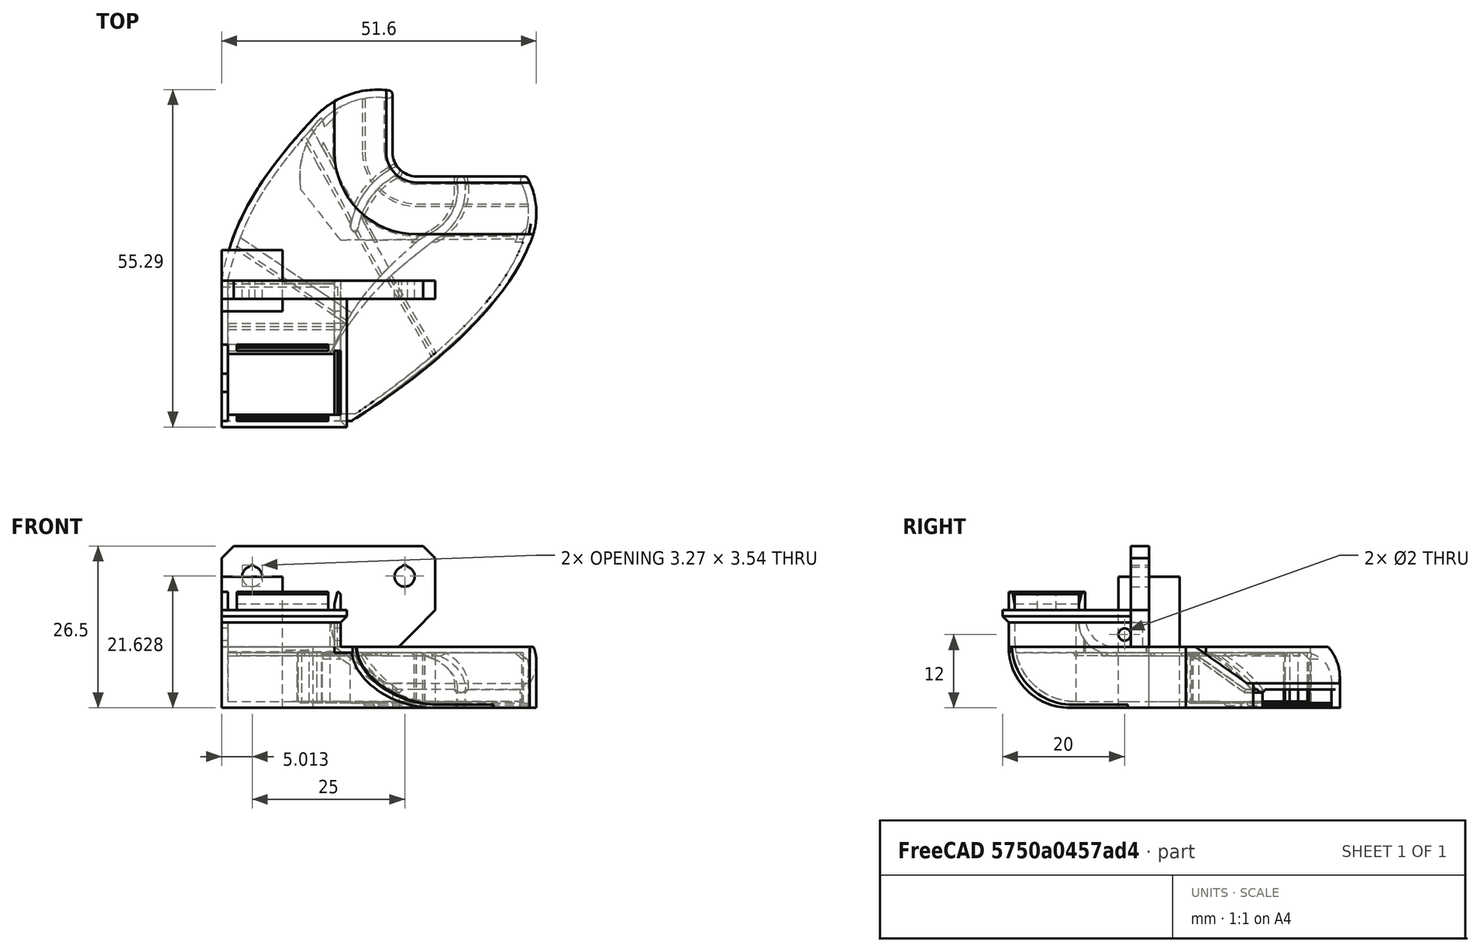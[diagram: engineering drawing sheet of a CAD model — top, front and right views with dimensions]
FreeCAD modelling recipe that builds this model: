
FCSTD DOCUMENT  (FreeCAD 0.18R16146 (Git))
Label: tidan-duct
License: All rights reserved
LicenseURL: http://en.wikipedia.org/wiki/All_rights_reserved
objects: Part::Box×37, Part::Cut×24, Part::Chamfer×18, Part::Feature×14, Part::MultiFuse×11, Part::Cylinder×6, Part::Fillet×6
note: 116 computed .brp shape members not serialized (recipe doc carries the construction recipe); baked Part::Feature solids carry a one-line shape summary decoded from their .brp

FEATURE [Part::Feature] Part__Feature034001  label="duct001"
  Placement = pos=(4.485,21.775,-6.0908e-11) rot=(0,0,-1;0.785398rad)
  shape: bbox 54.56 x 52.76 x 17.07 mm, 140 faces (baked)
FEATURE [Part::Box] Box  label="Cube"
  AttacherType = Attacher::AttachEngine3D
  Height = 10
  Length = 42
  Placement = pos=(-35,-33,10) rot=(0,0,1;0rad)
  Width = 47
FEATURE [Part::Cut] Cut
  Base = -> Part__Feature034001
  Tool = -> Box
FEATURE [Part::Box] Box001  label="Cube001"
  AttacherType = Attacher::AttachEngine3D
  Height = 31
  Length = 50
  Placement = pos=(-35,-32,-4) rot=(0,0,1;0rad)
  Width = 31
FEATURE [Part::Cut] Cut001
  Base = -> Cut
  Tool = -> Box001
FEATURE [Part::Box] Box002  label="Cube002"
  AttacherType = Attacher::AttachEngine3D
  Height = 16
  Length = 10
  Placement = pos=(-33.8,-4,0) rot=(0,0,1;0rad)
  Width = 10
FEATURE [Part::Cut] Cut002
  Base = -> Cut001
  Placement = pos=(-2.5,3.3,-9) rot=(0,0,1;0rad)
  Tool = -> Box002
FEATURE [Part::Box] Box005  label="Cube005"
  AttacherType = Attacher::AttachEngine3D
  Height = 10
  Length = 35
  Width = 3
FEATURE [Part::Cylinder] Cylinder
  Angle = 360
  AttacherType = Attacher::AttachEngine3D
  Height = 10
  Placement = pos=(5,1e-15,5) rot=(-1,0,0;1.5708rad)
  Radius = 1.65
FEATURE [Part::Cylinder] Cylinder001
  Angle = 360
  AttacherType = Attacher::AttachEngine3D
  Height = 10
  Placement = pos=(30,1e-15,5) rot=(-1,0,0;1.5708rad)
  Radius = 1.65
FEATURE [Part::Cylinder] Cylinder002
  Angle = 360
  AttacherType = Attacher::AttachEngine3D
  Height = 10
  Placement = pos=(30,1e-15,5) rot=(-1,0,0;1.5708rad)
  Radius = 0.5
FEATURE [Part::Cylinder] Cylinder003
  Angle = 360
  AttacherType = Attacher::AttachEngine3D
  Height = 10
  Placement = pos=(5,1e-15,5) rot=(-1,0,0;1.5708rad)
  Radius = 0.5
FEATURE [Part::MultiFuse] Fusion001
  Shapes = -> [Cylinder001,Cylinder]
FEATURE [Part::MultiFuse] Fusion002
  Placement = pos=(0,0,1.4) rot=(0,0,1;0rad)
  Shapes = -> [Cylinder003,Cylinder002]
FEATURE [Part::MultiFuse] Fusion003
  Shapes = -> [Fusion002,Fusion001]
FEATURE [Part::Chamfer] Chamfer001
  Base = -> Box005
  Edges = 2 edges r=2: [Edge2,Edge6]
FEATURE [Part::Cut] Cut003  label="mounter"
  Base = -> Chamfer001
  Placement = pos=(-38,-7,10) rot=(0,0,1;0rad)
  Tool = -> Fusion003
FEATURE [Part::Box] Box011  label="Cube011"
  AttacherType = Attacher::AttachEngine3D
  Height = 3
  Length = 15
  Placement = pos=(0,-22.5,0) rot=(0,0,1;0rad)
  Width = 1
FEATURE [Part::Box] Box012  label="Cube012"
  AttacherType = Attacher::AttachEngine3D
  Height = 3
  Length = 1
  Placement = pos=(16,-33,0) rot=(0,0,1;0rad)
  Width = 10.5
FEATURE [Part::Box] Box013  label="Cube013"
  AttacherType = Attacher::AttachEngine3D
  Height = 3
  Length = 15
  Placement = pos=(0,-34,0) rot=(0,0,1;0rad)
  Width = 1
FEATURE [Part::Box] Box014  label="Cube014"
  AttacherType = Attacher::AttachEngine3D
  Height = 3
  Length = 1
  Placement = pos=(-2.5,-34,0) rot=(0,0,1;0rad)
  Width = 4.75
FEATURE [Part::Box] Box015  label="Cube015"
  AttacherType = Attacher::AttachEngine3D
  Height = 3
  Length = 1
  Placement = pos=(-2.5,-26.25,0) rot=(0,0,1;0rad)
  Width = 4.75
FEATURE [Part::Box] Box016  label="Cube016"
  AttacherType = Attacher::AttachEngine3D
  Height = 2
  Length = 20.5
  Placement = pos=(-2.5,-35,-2) rot=(0,0,1;0rad)
  Width = 13.5
FEATURE [Part::Box] Box017  label="Cube017"
  AttacherType = Attacher::AttachEngine3D
  Height = 2
  Length = 20.5
  Placement = pos=(-38,-16,7.5) rot=(0,0,1;0rad)
  Width = 12
FEATURE [Part::Chamfer] Chamfer002
  Base = -> Box011
  Edges = 1 edges: [Edge10 r1=2 r2=0.5]
FEATURE [Part::Chamfer] Chamfer003
  Base = -> Box013
  Edges = 1 edges: [Edge12 r1=2 r2=0.4]
FEATURE [Part::Chamfer] Chamfer004
  Base = -> Box012
  Edges = 1 edges: [Edge2 r1=2 r2=0.5]
FEATURE [Part::Chamfer] Chamfer005
  Base = -> Chamfer004
  Edges = 1 edges r=0.4: [Edge15]
FEATURE [Part::Chamfer] Chamfer006
  Base = -> Chamfer003
  Edges = 1 edges r=0.4: [Edge7]
FEATURE [Part::Chamfer] Chamfer007
  Base = -> Chamfer002
  Edges = 1 edges r=0.4: [Edge13]
FEATURE [Part::Box] Box018  label="Cube018"
  AttacherType = Attacher::AttachEngine3D
  Height = 2
  Length = 17.5
  Placement = pos=(-1.5,-33,-2) rot=(0,0,1;0rad)
  Width = 10.5
FEATURE [Part::Cut] Cut004
  Base = -> Box016
  Tool = -> Box018
FEATURE [Part::MultiFuse] Fusion004002002
  Placement = pos=(-35.5,7,9.5) rot=(0,0,1;0rad)
  Shapes = -> [Box015,Chamfer007,Chamfer006,Chamfer005,Cut004,Box014]
FEATURE [Part::Feature] Body001001  label="Body002"
  Placement = pos=(0,0,-9) rot=(0,0,1;0rad)
  shape: bbox 32 x 33 x 12 mm, 6 faces (baked)
FEATURE [Part::Feature] Body001002  label="Body003"
  Placement = pos=(0,0,-9) rot=(0,0,1;0rad)
  shape: bbox 16 x 26.5 x 13 mm, 6 faces (baked)
FEATURE [Part::Box] Box021  label="Cube021"
  AttacherType = Attacher::AttachEngine3D
  Height = 18
  Length = 52
  Placement = pos=(-38,-28,-9) rot=(0,0,1;0rad)
  Width = 2
FEATURE [Part::Box] Box022  label="Cube022"
  AttacherType = Attacher::AttachEngine3D
  Height = 1
  Length = 52
  Placement = pos=(-38,-27,-9) rot=(0,0,1;0rad)
  Width = 20
FEATURE [Part::Feature] Fusion004002003
  shape: bbox 52 x 20 x 18 mm, 8 faces (baked)
FEATURE [Part::Fillet] Fillet
  Base = -> Fusion004002003
  Edges = 1 edges r=10: [Edge7]
FEATURE [Part::Fillet] Fillet002
  Base = -> Fillet
  Edges = 1 edges r=10: [Edge21]
FEATURE [Part::MultiFuse] Fusion
  Shapes = -> [Box021,Box022]
FEATURE [Part::Fillet] Fillet003
  Base = -> Fusion
  Edges = 1 edges r=10: [Edge11]
  Placement = pos=(0,-0.5,-0.5) rot=(0,0,1;0rad)
FEATURE [Part::Feature] Fillet003001  label="Fillet004"
  Placement = pos=(0,-0.5,-0.5) rot=(0,0,1;0rad)
  shape: bbox 52 x 21 x 18 mm, 15 faces (baked)
FEATURE [Part::Cut] Cut005
  Base = -> Body001001
  Tool = -> Fillet003001
FEATURE [Part::Box] Box023  label="Cube023"
  AttacherType = Attacher::AttachEngine3D
  Height = 18
  Length = 1
  Placement = pos=(-38,-27,-9) rot=(0,0,1;0rad)
  Width = 23
FEATURE [Part::Box] Box024  label="Cube024"
  AttacherType = Attacher::AttachEngine3D
  Height = 10
  Length = 42
  Placement = pos=(-43,-12,1) rot=(0,0,1;0rad)
  Width = 41
FEATURE [Part::Box] Box025  label="Cube025"
  AttacherType = Attacher::AttachEngine3D
  Height = 10
  Length = 42
  Placement = pos=(-18,-32,1) rot=(0,0,1;0rad)
  Width = 41
FEATURE [Part::Cut] Cut007
  Base = -> Cut005
  Tool = -> Box025
FEATURE [Part::Chamfer] Chamfer
  Base = -> Cut007
  Edges = 1 edges r=2: [Edge10]
FEATURE [Part::Cut] Cut008
  Base = -> Body001002
  Tool = -> Box024
FEATURE [Part::Chamfer] Chamfer008
  Base = -> Chamfer
  Edges = 1 edges r=0.4: [Edge1]
FEATURE [Part::Feature] Body001001001  label="Body004"
  Placement = pos=(1,0,-11) rot=(0,0,1;0rad)
  shape: bbox 32 x 33 x 12 mm, 6 faces (baked)
FEATURE [Part::Feature] Body001001002  label="Body005"
  Placement = pos=(1,0,-2) rot=(0,0,1;0rad)
  shape: bbox 32 x 33 x 12 mm, 6 faces (baked)
FEATURE [Part::MultiFuse] Fusion004002004
  Shapes = -> [Body001001002,Body001001001]
FEATURE [Part::Cut] Cut009
  Base = -> Fillet002
  Tool = -> Fusion004002004
FEATURE [Part::Feature] Pad002001  label="Pad003"
  Placement = pos=(0,0,-13) rot=(0,0,1;0rad)
  shape: bbox 37.34 x 24.4 x 27 mm, 14 faces (baked)
FEATURE [Part::Cut] Cut010
  Base = -> Cut009
  Tool = -> Pad002001
FEATURE [Part::Feature] Pad002002001  label="Pad002003"
  shape: bbox 50.43 x 49.62 x 1 mm, 36 faces (baked)
FEATURE [Part::Cut] Cut011
  Base = -> Box023
  Tool = -> Fillet003
FEATURE [Part::Feature] Fusion004002006001  label="Fusion004002007"
  shape: bbox 20.5 x 11 x 10 mm, 8 faces (baked)
FEATURE [Part::Fillet] Fillet003002
  Base = -> Fusion004002006001
  Edges = 1 edges r=5: [Edge7]
FEATURE [Part::Fillet] Fillet003003
  Base = -> Fillet003002
  Edges = 1 edges r=5: [Edge21]
FEATURE [Part::Box] Box028  label="Cube028"
  AttacherType = Attacher::AttachEngine3D
  Height = 10
  Length = 1
  Placement = pos=(-19.5,-27,0) rot=(0,0,1;0rad)
  Width = 23
FEATURE [Part::Box] Box029  label="Cube029"
  AttacherType = Attacher::AttachEngine3D
  Height = 10
  Length = 7
  Placement = pos=(-19.5,-27,1) rot=(0,0,1;0rad)
  Width = 23
FEATURE [Part::Cut] Cut012
  Base = -> Cut010
  Tool = -> Box029
FEATURE [Part::Box] Box030  label="Cube030"
  AttacherType = Attacher::AttachEngine3D
  Height = 1
  Length = 3
  Placement = pos=(-19.5,-27,0) rot=(0,0,1;0rad)
  Width = 23
FEATURE [Part::Box] Box031  label="Cube031"
  AttacherType = Attacher::AttachEngine3D
  Height = 10
  Length = 1
  Placement = pos=(-18.5,-27,1) rot=(0,0,1;0rad)
  Width = 23
FEATURE [Part::Cut] Cut013
  Base = -> Fillet003003
  Tool = -> Box031
FEATURE [Part::MultiFuse] Fusion004002006002
  Shapes = -> [Box028,Box030]
FEATURE [Part::Feature] Body001001003  label="Body006"
  Placement = pos=(0,0,-8) rot=(0,0,1;0rad)
  shape: bbox 7.895 x 21.33 x 5 mm, 13 faces (baked)
FEATURE [Part::Feature] Body001001004  label="Body007"
  Placement = pos=(0,0,-5) rot=(0,0,1;0rad)
  shape: bbox 7.895 x 21.33 x 5 mm, 13 faces (baked)
FEATURE [Part::Cut] Cut014
  Base = -> Cut002
  Tool = -> Body001001003
FEATURE [Part::Cut] Cut015
  Base = -> Cut014
  Tool = -> Body001001004
FEATURE [Part::Box] Box032  label="Cube032"
  AttacherType = Attacher::AttachEngine3D
  Height = 2
  Length = 10
  Placement = pos=(-28,-1,-8) rot=(0,0,1;0rad)
  Width = 15
FEATURE [Part::Cut] Cut016
  Base = -> Cut015
  Tool = -> Box032
FEATURE [Part::Feature] Body001001005  label="Body008"
  Placement = pos=(0,0,-9) rot=(0,0,1;0rad)
  shape: bbox 49.61 x 30.51 x 1 mm, 16 faces (baked)
FEATURE [Part::Box] Box033  label="Cube033"
  AttacherType = Attacher::AttachEngine3D
  Height = 1
  Length = 4
  Placement = pos=(-27,2,-9) rot=(0,0,1;0rad)
  Width = 4
FEATURE [Part::MultiFuse] Fusion004002006003
  Shapes = -> [Body001001005,Box033]
FEATURE [Part::Feature] Body001001006  label="Body009"
  Placement = pos=(0,0,-8.5) rot=(0,0,1;0rad)
  shape: bbox 17.67 x 19.56 x 20 mm, 5 faces (baked)
FEATURE [Part::Chamfer] Chamfer009
  Base = -> Body001001006
  Edges = 1 edges: [Edge1 r1=2 r2=0.2]
FEATURE [Part::Box] Box034  label="Cube034"
  AttacherType = Attacher::AttachEngine3D
  Height = 33
  Length = 31
  Placement = pos=(-29,-12.5,0.5) rot=(0,0,1;0rad)
  Width = 29
FEATURE [Part::Cut] Cut017
  Base = -> Chamfer009
  Tool = -> Box034
FEATURE [Part::Box] Box035  label="Cube035"
  AttacherType = Attacher::AttachEngine3D
  Height = 11
  Length = 18
  Placement = pos=(-29,-19.5,8.5) rot=(0,0,1;0rad)
  Width = 10
FEATURE [Part::Box] Box036  label="Cube036"
  AttacherType = Attacher::AttachEngine3D
  Height = 32
  Length = 18
  Placement = pos=(-29,-26,-9) rot=(0,0,1;0rad)
  Width = 10
FEATURE [Part::Cut] Cut018
  Base = -> Cut017
  Tool = -> Box036
FEATURE [Part::Box] Box037  label="Cube037"
  AttacherType = Attacher::AttachEngine3D
  Height = 15
  Length = 10
  Placement = pos=(-24,-13.5,5.5) rot=(0,0,1;0rad)
  Width = 10
FEATURE [Part::Cut] Cut019
  Base = -> Cut018
  Tool = -> Box035
FEATURE [Part::Fillet] Fillet003004
  Base = -> Box037
  Edges = 1 edges r=5: [Edge9]
  Placement = pos=(0,-2,-5.5) rot=(0,0,1;0rad)
FEATURE [Part::Cut] Cut020
  Base = -> Cut019
  Tool = -> Fillet003004
FEATURE [Part::Box] Box038  label="Cube038"
  AttacherType = Attacher::AttachEngine3D
  Height = 1
  Length = 2
  Placement = pos=(-17.3285,-11.2731,-0.5) rot=(0,0,1;0.977384rad)
  Width = 23
FEATURE [Part::Box] Box039  label="Cube039"
  AttacherType = Attacher::AttachEngine3D
  Height = 1
  Length = 2
  Placement = pos=(-11.7994,-3.80881,-0.5) rot=(0,0,1;0.506145rad)
  Width = 27
FEATURE [Part::Chamfer] Chamfer010
  Base = -> Box038
  Edges = 1 edges r=0.5: [Edge4]
FEATURE [Part::Chamfer] Chamfer011
  Base = -> Box039
  Edges = 1 edges r=0.5: [Edge4]
FEATURE [Part::Box] Box040  label="Cube040"
  AttacherType = Attacher::AttachEngine3D
  Height = 3
  Length = 35
  Placement = pos=(-38,-7,7.5) rot=(0,0,1;0rad)
  Width = 3
FEATURE [Part::Box] Box041  label="Cube041"
  AttacherType = Attacher::AttachEngine3D
  Height = 10
  Length = 19
  Placement = pos=(-38,-5,0) rot=(0,0,1;0rad)
  Width = 1
FEATURE [Part::Chamfer] Chamfer012
  Base = -> Fusion004002002
  Edges = 2 edges r=1: [Edge27,Edge46]
FEATURE [Part::Chamfer] Chamfer013
  Base = -> Box017
  Edges = 1 edges r=1: [Edge8]
FEATURE [Part::Chamfer] Chamfer014
  Base = -> Box040
  Edges = 1 edges r=2: [Edge8]
FEATURE [Part::MultiFuse] Fusion004002006004  label="mounter-fixed"
  Shapes = -> [Chamfer014,Chamfer013,Chamfer012,Cut003]
FEATURE [Part::Cylinder] Cylinder004
  Angle = 360
  AttacherType = Attacher::AttachEngine3D
  Height = 35
  Placement = pos=(-9,-8,3) rot=(0,-1,0;1.5708rad)
  Radius = 1
FEATURE [Part::Cylinder] Cylinder005
  Angle = 360
  AttacherType = Attacher::AttachEngine3D
  Height = 35
  Placement = pos=(-9,-8,3) rot=(0,-1,0;1.5708rad)
  Radius = 1
FEATURE [Part::Cut] Cut021
  Base = -> Cut011
  Tool = -> Cylinder004
FEATURE [Part::Cut] Cut022
  Base = -> Fusion004002006002
  Tool = -> Cylinder005
FEATURE [Part::Box] Box043  label="Cube043"
  AttacherType = Attacher::AttachEngine3D
  Height = 1
  Length = 20
  Placement = pos=(-37.5,-12,-0.5) rot=(0,0,1;0rad)
  Width = 1
FEATURE [Part::Chamfer] Chamfer016
  Base = -> Box043
  Edges = 1 edges r=0.5: [Edge9]
FEATURE [Part::Box] Box044  label="Cube044"
  AttacherType = Attacher::AttachEngine3D
  Height = 1
  Length = 15.5
  Placement = pos=(-11.2452,-3.31699,-0.5) rot=(0,0,-1;1.0472rad)
  Width = 1
FEATURE [Part::Chamfer] Chamfer017
  Base = -> Box044
  Edges = 1 edges r=0.5: [Edge9]
FEATURE [Part::Box] Box042  label="Cube042"
  AttacherType = Attacher::AttachEngine3D
  Height = 9
  Length = 14.5
  Placement = pos=(-19,-7,0) rot=(0,0,1;0rad)
  Width = 3
FEATURE [Part::Chamfer] Chamfer018
  Base = -> Box042
  Edges = 1 edges r=8: [Edge8]
FEATURE [Part::MultiFuse] Fusion004002006005
  Shapes = -> [Fusion004002006004,Chamfer018,Box041]
FEATURE [Part::Box] Box045  label="Cube045"
  AttacherType = Attacher::AttachEngine3D
  Height = 23
  Length = 52
  Placement = pos=(-38,-38.5,-19.5) rot=(0,0,1;0rad)
  Width = 59
FEATURE [Part::MultiFuse] Fusion004002006006
  Placement = pos=(0,0,2.5) rot=(0,0,1;0rad)
  Shapes = -> [Cut008,Chamfer008,Pad002002001,Cut012,Cut013,Cut016,Fusion004002006003,Cut020,Chamfer010,Chamfer011,Cut021,Cut022,Chamfer016,Chamfer017]
FEATURE [Part::Box] Box046  label="Cube046"
  AttacherType = Attacher::AttachEngine3D
  Height = 23
  Length = 52
  Placement = pos=(-38,-38.5,7.5) rot=(0,0,1;0rad)
  Width = 59
FEATURE [Part::Box] Box047  label="Cube047"
  AttacherType = Attacher::AttachEngine3D
  Height = 21.5
  Length = 10
  Placement = pos=(-38,-9,-6.5) rot=(0,0,1;0rad)
  Width = 10
FEATURE [Part::Cut] Cut023
  Base = -> Fusion004002006006
  Tool = -> Box046
FEATURE [Part::Cut] Cut024
  Base = -> Fusion004002006005
  Tool = -> Box045
